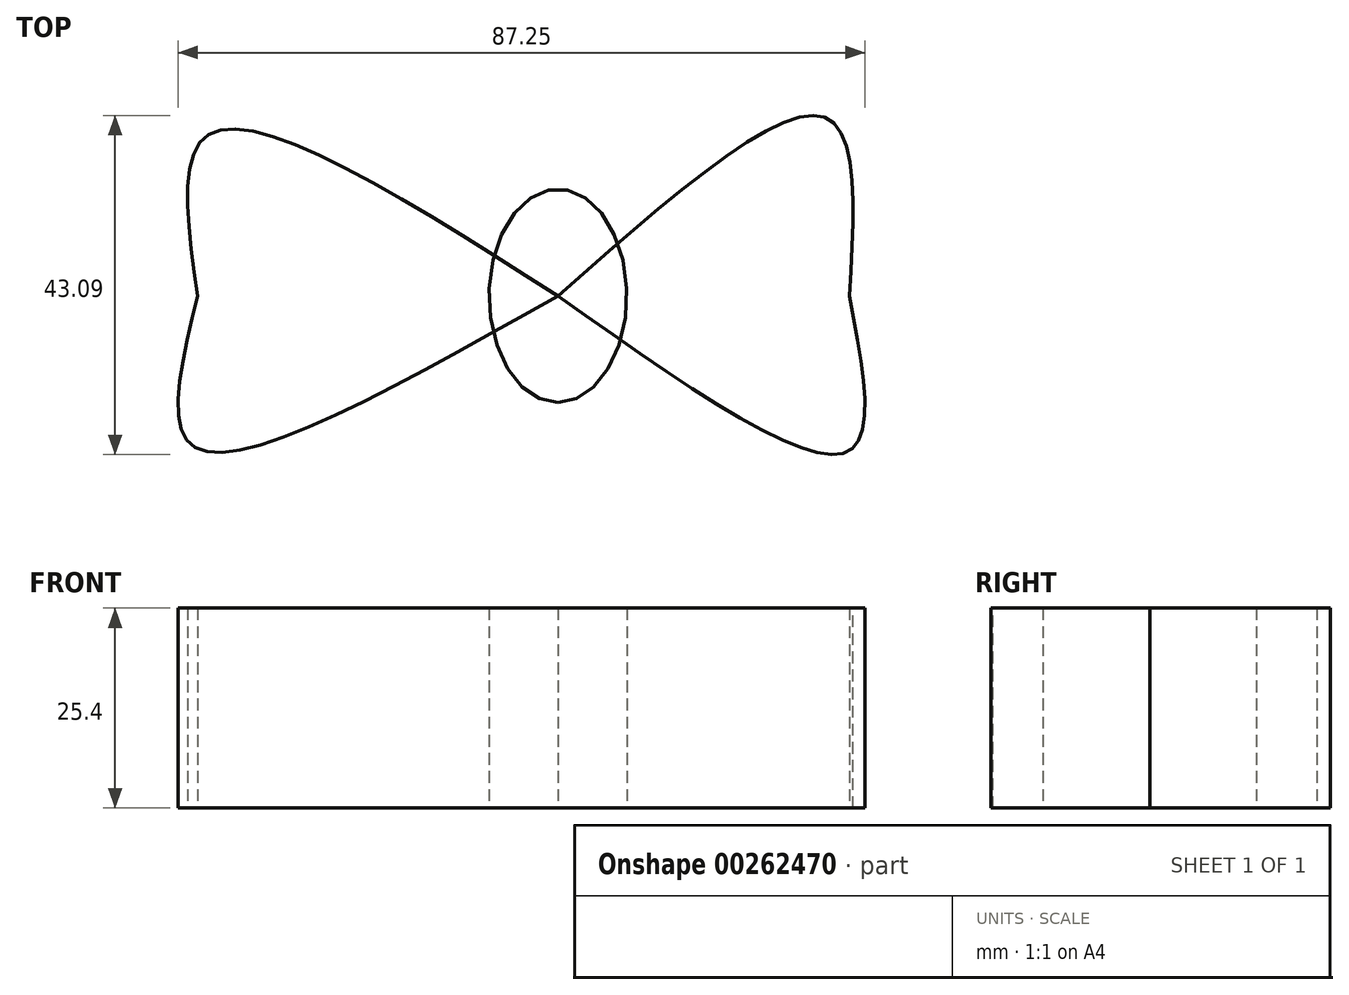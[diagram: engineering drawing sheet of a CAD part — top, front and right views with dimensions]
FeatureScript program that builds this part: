
annotation { "Feature Type Name" : "Feature", "Feature Type Description" : "" }
export const myFeature = defineFeature(function(context is Context, id is Id, definition is map)
    precondition{}
    {
        {
            var Q0;
            Q0=qCreatedBy(makeId("Top.planeOp"),FACE);
            var sketch = newSketch(context, id + "F0", { "sketchPlane" : qUnion([Q0])});
            skEllipse(sketch, "E0", {"center": v(0, 0) * mm, "majorRadius": 13.55 * mm, "minorRadius": 8.74 * mm, "majorAxis": v(0, -1)});
            skSolve(sketch);
        }
        {
            var Q0;
            Q0=qCreatedBy(makeId("Top.planeOp"),FACE);
            var sketch = newSketch(context, id + "F1", { "sketchPlane" : qUnion([Q0])});
            skFitSpline(sketch, "E1", {"points": [v(0, 0) * mm, v(-46.34, -19.1) * mm, v(-45.76, 0) * mm], "startDerivative": vector(-98.6, -55.89) * mm, "endDerivative": vector(16.12, 65.46) * mm});
            skFitSpline(sketch, "E2", {"points": [v(0, 0) * mm, v(-44.3, 20.55) * mm, v(-45.76, 0) * mm], "startDerivative": vector(-94.1, 59.99) * mm, "endDerivative": vector(9.96, -69.14) * mm});
            skFitSpline(sketch, "E3", {"points": [v(0, 0) * mm, v(37.02, -19.67) * mm, v(37.02, 0) * mm], "startDerivative": vector(80.89, -57.35) * mm, "endDerivative": vector(-12.68, 64.97) * mm});
            skFitSpline(sketch, "E4", {"points": [v(0, 0) * mm, v(34.1, 22.59) * mm, v(37.02, 0) * mm], "startDerivative": vector(74.65, 65.88) * mm, "endDerivative": vector(-4.45, -72.58) * mm});
            skSolve(sketch);
        }
        {
            var Q0;
            Q0 = qSketchRegion(id + "F1", true);
            var Q1;
            Q1 = qSketchRegion(id + "F0", true);
            extrude(context, id + "F2", {"entities" : qUnion([Q0, Q1]), "depth" : 25.4 * mm});
        }
        {
            var Q0;
            Q0 = qSketchRegion(id + "F0", true);
            extrude(context, id + "F3", {"entities" : qUnion([Q0]), "depth" : 25.4 * mm});
        }
    });
